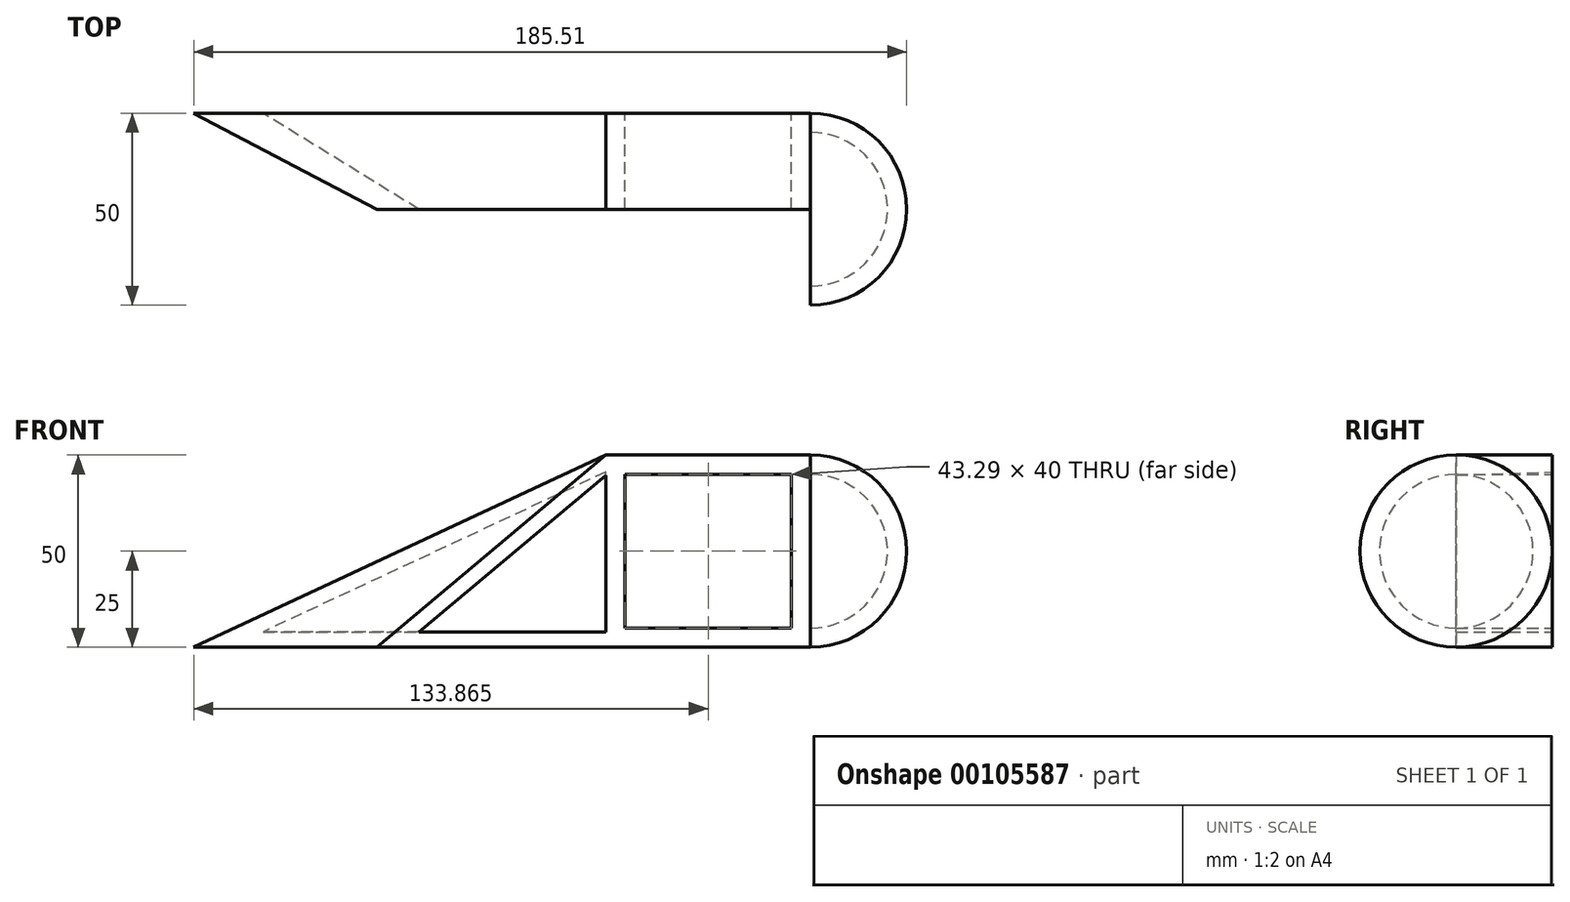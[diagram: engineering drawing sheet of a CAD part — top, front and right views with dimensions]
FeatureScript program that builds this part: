
annotation { "Feature Type Name" : "Feature", "Feature Type Description" : "" }
export const myFeature = defineFeature(function(context is Context, id is Id, definition is map)
    precondition{}
    {
        {
            var Q0;
            Q0=qCreatedBy(makeId("Front.planeOp"),FACE);
            var sketch = newSketch(context, id + "F0", { "sketchPlane" : qUnion([Q0])});
            skLineSegment(sketch, "E0.bottom", {"start": v(0, 0) * mm, "end": v(-53.29, 0) * mm});
            skLineSegment(sketch, "E0.top", {"start": v(0, 50) * mm, "end": v(-53.29, 50) * mm});
            skLineSegment(sketch, "E0.left", {"start": v(0, 0) * mm, "end": v(0, 50) * mm});
            skLineSegment(sketch, "E0.right", {"start": v(-53.29, 0) * mm, "end": v(-53.29, 50) * mm});
            skLineSegment(sketch, "E1.bottom", {"start": v(-48.29, 45) * mm, "end": v(-5, 45) * mm});
            skLineSegment(sketch, "E1.top", {"start": v(-48.29, 5) * mm, "end": v(-5, 5) * mm});
            skLineSegment(sketch, "E1.left", {"start": v(-48.29, 45) * mm, "end": v(-48.29, 5) * mm});
            skLineSegment(sketch, "E1.right", {"start": v(-5, 45) * mm, "end": v(-5, 5) * mm});
            skSolve(sketch);
        }
        {
            var Q0;
            Q0 = qSketchRegion(id + "F0", true);
            extrude(context, id + "F1", {"entities" : qUnion([Q0]), "depth" : 25 * mm});
        }
        {
            var Q0;
            Q0=makeQuery(id+"F1.opExtrude","CAP_FACE",FACE,{"disambiguationData":[OSD([sQuery(id+"F0.wireOp",EDGE,"E0.bottom"),sQuery(id+"F0.wireOp",EDGE,"E0.top"),sQuery(id+"F0.wireOp",EDGE,"E0.left"),sQuery(id+"F0.wireOp",EDGE,"E0.right"),sQuery(id+"F0.wireOp",EDGE,"E1.bottom"),sQuery(id+"F0.wireOp",EDGE,"E1.top"),sQuery(id+"F0.wireOp",EDGE,"E1.left"),sQuery(id+"F0.wireOp",EDGE,"E1.right")])],"isStart":false});
            var sketch = newSketch(context, id + "F2", { "sketchPlane" : qUnion([Q0])});
            skCircle(sketch, "E2", {"center": v(0, 25) * mm, "radius": 25 * mm});
            skLineSegment(sketch, "E3", {"start": v(0, 50) * mm, "end": v(0, 0) * mm});
            skLineSegment(sketch, "E4", {"start": v(-53.29, 50) * mm, "end": v(-112.88, 0) * mm});
            skLineSegment(sketch, "E5", {"start": v(-112.88, 0) * mm, "end": v(-53.29, 0) * mm});
            skLineSegment(sketch, "E6", {"start": v(-53.29, 0) * mm, "end": v(-53.29, 50) * mm});
            skCircle(sketch, "E7.0", {"center": v(0, 25) * mm, "radius": 20 * mm});
            skLineSegment(sketch, "E8.0", {"start": v(-101.89, 4) * mm, "end": v(-53.29, 4) * mm});
            skLineSegment(sketch, "E8.1", {"start": v(-50.72, 46.94) * mm, "end": v(-101.89, 4) * mm});
            skSolve(sketch);
        }
        {
            var Q0;
            {var subQ0=sQuery(id+"F2.wireOp",EDGE,"E3");var subQ4=sQuery(id+"F2.wireOp",EDGE,"E7.0");var subQ5=makeQuery(id+"F2.imprint","INTERSECT",VERTEX,{"disambiguationData":[OD(0.0)],"derivedFrom":[subQ0,subQ4]});Q0=makeQuery(id+"F2.imprint","IMPRINT",FACE,{"disambiguationData":[TD([[makeQuery(id+"F2.imprint","IMPRINT",EDGE,{"disambiguationData":[TD([[subQ5,-1.0]])],"derivedFrom":subQ4}),-1.0]])]});}
            var Q1;
            Q1=sQuery(id+"F2.wireOp",EDGE,"E3");
            revolve(context, id + "F3", {"operationType" : NewBodyOperationType.ADD, "entities" : qUnion([Q0]), "axis" : qUnion([Q1]), "revolveType" : RevolveType.SYMMETRIC, "angle" : 180 * degree});
        }
        {
            var Q0;
            Q0=makeQuery(id+"F1.opExtrude","CAP_FACE",FACE,{"disambiguationData":[OSD([sQuery(id+"F0.wireOp",EDGE,"E0.bottom"),sQuery(id+"F0.wireOp",EDGE,"E0.top"),sQuery(id+"F0.wireOp",EDGE,"E0.left"),sQuery(id+"F0.wireOp",EDGE,"E0.right"),sQuery(id+"F0.wireOp",EDGE,"E1.bottom"),sQuery(id+"F0.wireOp",EDGE,"E1.top"),sQuery(id+"F0.wireOp",EDGE,"E1.left"),sQuery(id+"F0.wireOp",EDGE,"E1.right")])],"isStart":true});
            var sketch = newSketch(context, id + "F4", { "sketchPlane" : qUnion([Q0])});
            skLineSegment(sketch, "E9", {"start": v(53.29, 50) * mm, "end": v(160.51, 0) * mm});
            skLineSegment(sketch, "E10", {"start": v(160.51, 0) * mm, "end": v(53.29, 0) * mm});
            skLineSegment(sketch, "E11", {"start": v(53.29, 0) * mm, "end": v(53.29, 50) * mm});
            skLineSegment(sketch, "E12.0", {"start": v(142.47, 4) * mm, "end": v(53.29, 4) * mm});
            skLineSegment(sketch, "E12.1", {"start": v(51.6, 46.37) * mm, "end": v(142.47, 4) * mm});
            skSolve(sketch);
        }
        {
            var Q1;
            {var subQ1=sQuery(id+"F2.wireOp",EDGE,"E4");Q1=makeQuery(id+"F2.imprint","IMPRINT",FACE,{"disambiguationData":[TD([[makeQuery(id+"F2.imprint","IMPRINT",EDGE,{"derivedFrom":subQ1}),1.0]])]});}
            var Q2;
            {var subQ2=sQuery(id+"F4.wireOp",EDGE,"E9");Q2=makeQuery(id+"F4.imprint","IMPRINT",FACE,{"disambiguationData":[TD([[makeQuery(id+"F4.imprint","IMPRINT",EDGE,{"derivedFrom":subQ2}),-1.0]])]});}
            loft(context, id + "F5", {"operationType" : NewBodyOperationType.ADD, "sheetProfilesArray" : [{ "sheetProfileEntities" : qUnion([Q1]) }, { "sheetProfileEntities" : qUnion([Q2]) }]});
        }
    });
